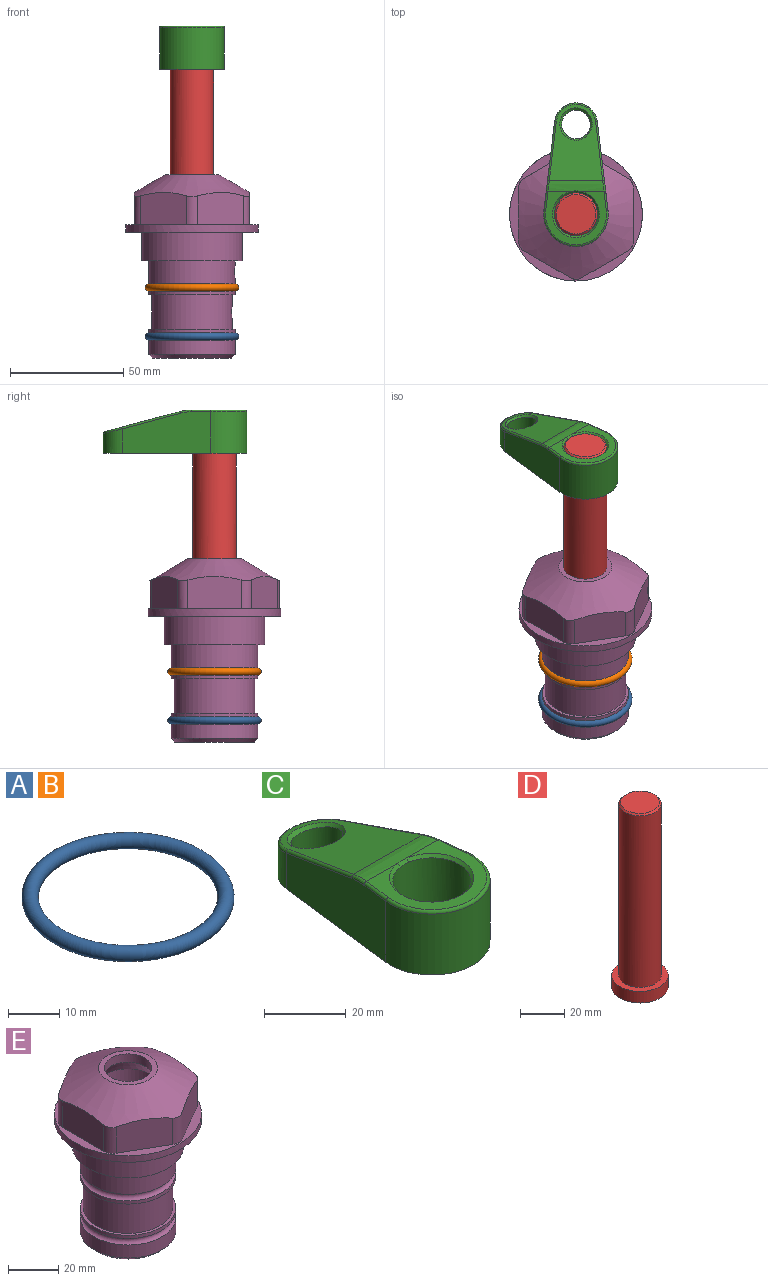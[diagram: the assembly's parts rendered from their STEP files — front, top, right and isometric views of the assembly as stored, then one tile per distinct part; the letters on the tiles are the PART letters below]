
ASSEMBLY  parts=5 mates=4
PART A: 1 faces, bbox 44.7x44.7x3.2 mm
  f0: torus R=19.05mm, axis (0,0,1), area 1193.9mm2
PART B: same geometry as A
PART C: 31 faces, bbox 31.7x65.5x19.8 mm
  f0: plane 39.12x18.26mm, normal (0.99,0.12,0), area 612.2mm2, adj f1,f4,f7,f11,f13,f15
  f1: cylinder r=9.53mm len=18.91mm, axis (0,0,-1), area 296.1mm2, adj f0,f2,f7,f17
  f2: plane 39.12x18.26mm, normal (-0.99,0.12,0), area 612.2mm2, adj f1,f4,f7,f12,f14,f16
  f3: cylinder r=6.35mm len=12.7mm, axis (0,0,-1), area 362.4mm2, adj f7,f18
  f4: cylinder r=14.29mm len=28.58mm, axis (0,0,-1), area 882.2mm2, adj f0,f2,f7,f10
  f5: cylinder r=9.53mm len=19.05mm, axis (0,0,-1), area 1092.6mm2, adj f7,f19,f20
  f6: plane 26.99x23.69mm, normal (0,0,1), area 216.2mm2, adj f9,f10,f11,f12,f19
  f7: plane 63.5x28.58mm, normal (0,0,-1), area 661.8mm2, adj f0,f1,f2,f3,f4,f5,f22,f23
  f8: plane 33.52x23.6mm, normal (0,0.26,0.97), area 486mm2, adj f9,f15,f16,f17,f18
  f9: cylinder r=19.05mm len=24.72mm, axis (1,0,0), area 120.4mm2, adj f6,f8,f13,f14,f20
  f10: torus R=13.49mm, axis (0,0,1), area 59mm2, adj f4,f6,f11,f12
  f11: cylinder r=0.79mm len=8.67mm, axis (0.12,-0.99,0), area 10.8mm2, adj f0,f6,f10,f13
  f12: cylinder r=0.79mm len=8.67mm, axis (0.12,0.99,0), area 10.8mm2, adj f2,f6,f10,f14
  f13: bspline ~4.95x1.42mm, area 6.1mm2, adj f0,f9,f11,f15
  f14: bspline ~4.95x1.42mm, area 6.1mm2, adj f2,f9,f12,f16
  f15: cylinder r=0.79mm len=25.95mm, axis (0.12,-0.96,0.26), area 32.9mm2, adj f0,f8,f13,f17
  f16: cylinder r=0.79mm len=25.95mm, axis (0.12,0.96,-0.26), area 32.9mm2, adj f2,f8,f14,f17
  f17: bspline ~18.91x8.38mm, area 30mm2, adj f1,f8,f15,f16
  f18: bspline ~14.29x14.29mm, area 48.3mm2, adj f3,f8
  f19: cone r=9.53mm half-angle=45deg, axis (0,0,1), area 66.5mm2, adj f5,f6,f20
  f20: bspline ~3.22x0.96mm, area 3.5mm2, adj f5,f9,f19
  f21: plane 2.75x2.72mm, normal (0,0,-1), area 2.9mm2, adj f23,f25,f28
  f22: plane 23.05x15.88mm, normal (-0.99,-0.12,0), area 323.6mm2, adj f7,f25,f26,f27,f28,f29
  f23: plane 23.05x15.88mm, normal (0.99,-0.12,0), area 323.6mm2, adj f7,f21,f25,f27,f28,f30
  f24: cylinder r=9.53mm len=10.69mm, axis (0,0,-1), area 114.7mm2, adj f7,f27,f29,f30
  f25: cylinder r=12.7mm len=20.59mm, axis (0,0,-1), area 381.1mm2, adj f7,f21,f22,f23,f26,f28
  f26: plane 2.75x2.72mm, normal (0,0,-1), area 2.9mm2, adj f22,f25,f28
  f27: plane 19.72x18.37mm, normal (0,-0.26,-0.97), area 291.8mm2, adj f22,f23,f24,f28,f29,f30
  f28: cylinder r=15.88mm len=19.92mm, axis (1,0,0), area 54.8mm2, adj f21,f22,f23,f25,f26,f27
  f29: cylinder r=1.59mm len=11mm, axis (0,0,-1), area 34.7mm2, adj f7,f22,f24,f27
  f30: cylinder r=1.59mm len=11mm, axis (0,0,-1), area 34.7mm2, adj f7,f23,f24,f27
PART D: 6 faces, bbox 25.4x25.4x101.6 mm
  f0: plane 17.46x17.46mm, normal (0,0,1), area 239.5mm2, adj f5
  f1: plane 25.4x25.4mm, normal (0,0,-1), area 506.7mm2, adj f2
  f2: cylinder r=12.7mm len=25.4mm, axis (0,0,1), area 506.7mm2, adj f1,f3
  f3: plane 25.4x25.4mm, normal (0,0,1), area 221.7mm2, adj f2,f4
  f4: cylinder r=9.53mm len=94.46mm, axis (0,0,1), area 5653mm2, adj f3,f5
  f5: cone r=8.73mm half-angle=45deg, axis (0,0,-1), area 64.4mm2, adj f0,f4
PART E: 36 faces, bbox 58.7x58.7x81 mm
  f0: cylinder r=17.78mm len=35.56mm, axis (0,0,1), area 1670.8mm2, adj f23,f24,f31
  f1: cylinder r=19.05mm len=38.1mm, axis (0,0,1), area 1191.9mm2, adj f26,f27,f30
  f2: plane 58.66x58.66mm, normal (0,0,-1), area 1150.6mm2, adj f3,f28
  f3: cylinder r=29.33mm len=58.66mm, axis (0,0,-1), area 585.1mm2, adj f2,f4
  f4: plane 58.66x58.66mm, normal (0,0,1), area 475.9mm2, adj f3,f5,f6,f7,f8,f9,f10,f11
  f5: plane 20.32x14.34mm, normal (-0.5,0.87,0), area 324.4mm2, adj f4,f15,f16,f17
  f6: plane 20.32x14.34mm, normal (0.5,0.87,0), area 324.4mm2, adj f4,f14,f15,f17
  f7: plane 23.48x14.34mm, normal (1,0,0), area 324.4mm2, adj f4,f13,f14,f17
  f8: plane 20.32x14.34mm, normal (0.5,-0.87,0), area 324.4mm2, adj f4,f12,f13,f17
  f9: plane 20.32x14.34mm, normal (-0.5,-0.87,0), area 324.4mm2, adj f4,f11,f12,f17
  f10: plane 23.48x14.34mm, normal (-1,0,0), area 324.4mm2, adj f4,f11,f16,f17
  f11: cylinder r=5.08mm len=12.85mm, axis (0,0,-1), area 67.2mm2, adj f4,f9,f10,f17
  f12: cylinder r=5.08mm len=12.85mm, axis (0,0,-1), area 67.2mm2, adj f4,f8,f9,f17
  f13: cylinder r=5.08mm len=12.85mm, axis (0,0,-1), area 67.2mm2, adj f4,f7,f8,f17
  f14: cylinder r=5.08mm len=12.85mm, axis (0,0,-1), area 67.2mm2, adj f4,f6,f7,f17
  f15: cylinder r=5.08mm len=12.85mm, axis (0,0,-1), area 67.2mm2, adj f4,f5,f6,f17
  f16: cylinder r=5.08mm len=12.85mm, axis (0,0,-1), area 67.2mm2, adj f4,f5,f10,f17
  f17: cone r=11.73mm half-angle=60deg, axis (0,0,-1), area 2071.8mm2, adj f5,f6,f7,f8,f9,f10,f11,f12
  f18: plane 23.46x23.46mm, normal (0,0,1), area 147.4mm2, adj f17,f35
  f19: plane 34.93x34.93mm, normal (0,0,-1), area 958mm2, adj f29
  f20: cylinder r=19.05mm len=38.1mm, axis (0,0,1), area 760.1mm2, adj f21,f29
  f21: torus R=19.05mm, axis (0,0,1), area 565.3mm2, adj f20,f22
  f22: cylinder r=19.05mm len=38.1mm, axis (0,0,1), area 190mm2, adj f21,f23
  f23: plane 38.1x38.1mm, normal (0,0,1), area 146.9mm2, adj f0,f22
  f24: plane 38.1x38.1mm, normal (0,0,-1), area 146.9mm2, adj f0,f25
  f25: cylinder r=19.05mm len=38.1mm, axis (0,0,1), area 190mm2, adj f24,f26
  f26: torus R=19.05mm, axis (0,0,1), area 565.3mm2, adj f1,f25
  f27: plane 44.45x44.45mm, normal (0,0,-1), area 411.7mm2, adj f1,f28
  f28: cylinder r=22.23mm len=44.45mm, axis (0,0,1), area 1773.5mm2, adj f2,f27
  f29: cone r=19.05mm half-angle=45deg, axis (0,0,1), area 257.5mm2, adj f19,f20
  f30: cylinder r=3.17mm len=6.75mm, axis (-1,0,0), area 128mm2, adj f1,f33
  f31: cylinder r=3.17mm len=6.35mm, axis (-1,0,0), area 102.5mm2, adj f0,f33
  f32: plane 25.4x25.4mm, normal (0,0,1), area 506.7mm2, adj f33
  f33: cylinder r=12.7mm len=66.42mm, axis (0,0,-1), area 5236.2mm2, adj f30,f31,f32,f34
  f34: cone r=9.53mm half-angle=30deg, axis (0,0,-1), area 443.4mm2, adj f33,f35
  f35: cylinder r=9.53mm len=19.05mm, axis (0,0,-1), area 240.9mm2, adj f18,f34
PLACE A t=(0,0,-21.59)mm
PLACE B at identity
PLACE C t=(0,0,27.55)mm
PLACE D rot(axis=(0,0,1),0deg) t=(0,0,27.55)mm
PLACE E at identity fixed
MATE cylindrical E.f0 <-> D.f2  axis (0,0,-1) through (0,0,-50.55)mm
MATE fastened A.f0 <-> E.f0  axis (0,0,1) through (0,0,-46.1)mm
MATE fastened D.f2 <-> C.f4  axis (0,0,1) through (0,0,91.05)mm
MATE fastened B.f0 <-> E.f0  axis (0,0,1) through (0,0,-24.51)mm
